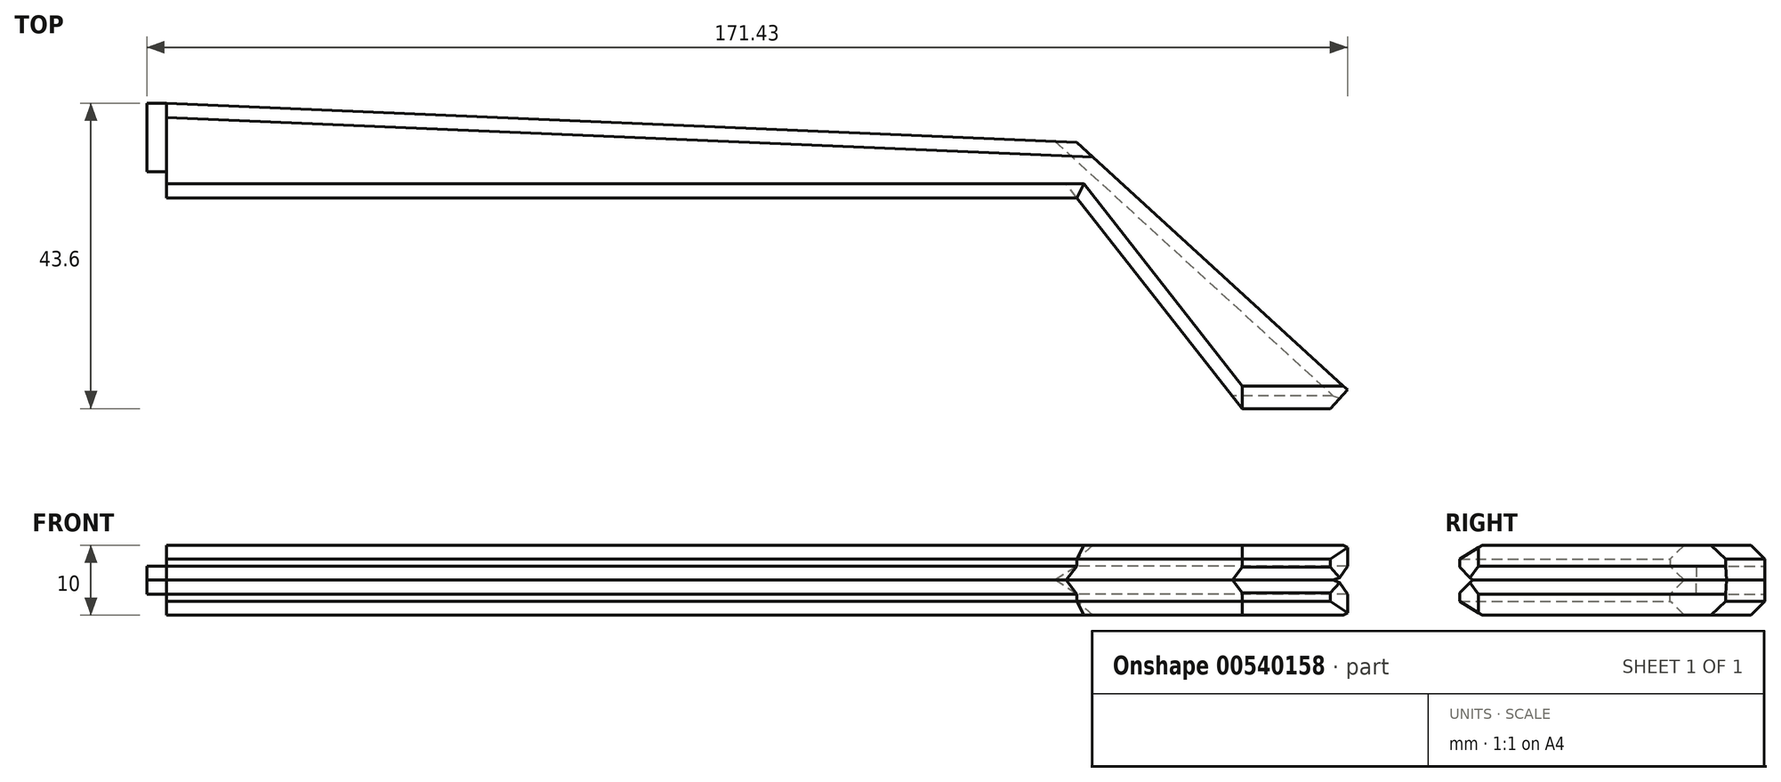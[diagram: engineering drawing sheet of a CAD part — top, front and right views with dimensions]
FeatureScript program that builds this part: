
annotation { "Feature Type Name" : "Feature", "Feature Type Description" : "" }
export const myFeature = defineFeature(function(context is Context, id is Id, definition is map)
    precondition{}
    {
        {
            var Q0;
            Q0=qCreatedBy(makeId("Top.planeOp"),FACE);
            var sketch = newSketch(context, id + "F0", { "sketchPlane" : qUnion([Q0])});
            skLineSegment(sketch, "E0", {"start": v(-80.29, 29.32) * mm, "end": v(49.71, 23.74) * mm});
            skLineSegment(sketch, "E1", {"start": v(49.71, 23.74) * mm, "end": v(88.34, -11.6) * mm});
            skLineSegment(sketch, "E2", {"start": v(88.34, -11.6) * mm, "end": v(85.75, -14.44) * mm});
            skLineSegment(sketch, "E3", {"start": v(85.75, -14.44) * mm, "end": v(73.34, -14.44) * mm});
            skLineSegment(sketch, "E4", {"start": v(73.34, -14.44) * mm, "end": v(73.34, -14.28) * mm});
            skLineSegment(sketch, "E5", {"start": v(73.34, -14.28) * mm, "end": v(49.71, 15.8) * mm});
            skLineSegment(sketch, "E6", {"start": v(49.71, 15.8) * mm, "end": v(-80.29, 15.8) * mm});
            skLineSegment(sketch, "E7", {"start": v(-80.29, 15.8) * mm, "end": v(-80.29, 29.32) * mm});
            skLineSegment(sketch, "E8", {"start": v(-80.29, 29.32) * mm, "end": v(-83.09, 29.32) * mm});
            skLineSegment(sketch, "E9", {"start": v(-83.09, 29.32) * mm, "end": v(-83.09, 19.52) * mm});
            skLineSegment(sketch, "E10", {"start": v(-83.09, 19.52) * mm, "end": v(-80.29, 19.52) * mm});
            skLineSegment(sketch, "E11", {"start": v(-80.29, 29.32) * mm, "end": v(-80.29, 19.52) * mm});
            skSolve(sketch);
        }
        {
            var Q0;
            {var subQ0=sQuery(id+"F0.wireOp",EDGE,"E0");Q0=makeQuery(id+"F0.imprint","IMPRINT",FACE,{"disambiguationData":[TD([[makeQuery(id+"F0.imprint","IMPRINT",EDGE,{"derivedFrom":subQ0}),-1.0]])]});}
            extrude(context, id + "F1", {"entities" : qUnion([Q0]), "depth" : 5 * mm, "offsetDistance" : 25 * mm});
        }
        {
            var Q0;
            Q0=makeQuery(id+"F1.opExtrude","CAP_EDGE",EDGE,{"disambiguationData":[OSD([sQuery(id+"F0.wireOp",EDGE,"E6")])],"isStart":true});
            var Q1;
            Q1=makeQuery(id+"F1.opExtrude","CAP_EDGE",EDGE,{"disambiguationData":[OSD([sQuery(id+"F0.wireOp",EDGE,"E1")])],"isStart":true});
            var Q2;
            Q2=makeQuery(id+"F1.opExtrude","CAP_EDGE",EDGE,{"disambiguationData":[OSD([sQuery(id+"F0.wireOp",EDGE,"E3")])],"isStart":true});
            var Q3;
            Q3=makeQuery(id+"F1.opExtrude","CAP_EDGE",EDGE,{"disambiguationData":[OSD([sQuery(id+"F0.wireOp",EDGE,"E5")])],"isStart":false});
            var Q4;
            Q4=makeQuery(id+"F1.opExtrude","CAP_EDGE",EDGE,{"disambiguationData":[OSD([sQuery(id+"F0.wireOp",EDGE,"E6")])],"isStart":false});
            var Q5;
            Q5=makeQuery(id+"F1.opExtrude","CAP_EDGE",EDGE,{"disambiguationData":[OSD([sQuery(id+"F0.wireOp",EDGE,"E0")])],"isStart":false});
            chamfer(context, id + "F2", {"entities" : qUnion([Q0, Q1, Q2, Q3, Q4, Q5]), "width" : 2 * mm, "tangentPropagation" : true});
        }
        {
            var Q0;
            Q0=makeQuery(id+"F0.imprint","IMPRINT",FACE,{"disambiguationData":[TD([[makeQuery(id+"F0.imprint","IMPRINT",EDGE,{"derivedFrom":sQuery(id+"F0.wireOp",EDGE,"E8")}),1.0]])]});
            extrude(context, id + "F3", {"entities" : qUnion([Q0]), "operationType" : NewBodyOperationType.ADD, "depth" : 2 * mm, "offsetDistance" : 25 * mm});
        }
        {
            var Q0;
            Q0=makeQuery(id+"F1.opExtrude","SWEPT_BODY",BODY,{"disambiguationData":[OSD([sQuery(id+"F0.wireOp",EDGE,"E0"),sQuery(id+"F0.wireOp",EDGE,"E1"),sQuery(id+"F0.wireOp",EDGE,"E2"),sQuery(id+"F0.wireOp",EDGE,"E3"),sQuery(id+"F0.wireOp",EDGE,"E4"),sQuery(id+"F0.wireOp",EDGE,"E5"),sQuery(id+"F0.wireOp",EDGE,"E6"),sQuery(id+"F0.wireOp",EDGE,"E7"),sQuery(id+"F0.wireOp",EDGE,"E11")])]});
            var Q1;
            Q1=qCreatedBy(makeId("Top.planeOp"),FACE);
            mirror(context, id + "F4", {"entities" : qUnion([Q0]), "mirrorPlane" : qUnion([Q1])});
        }
        {
            var Q0;
            Q0=makeQuery(id+"F1.opExtrude","SWEPT_FACE",FACE,{"disambiguationData":[OSD([sQuery(id+"F0.wireOp",EDGE,"E4")])]});
            extrude(context, id + "F5", {"entities" : qUnion([Q0]), "operationType" : NewBodyOperationType.REMOVE, "oppositeDirection" : true, "depth" : 25 * mm, "offsetDistance" : 25 * mm});
        }
        {
            var Q0;
            Q0=makeQuery(id+"F4.opPattern","COPY",FACE,{"derivedFrom":makeQuery(id+"F1.opExtrude","SWEPT_FACE",FACE,{"disambiguationData":[OSD([sQuery(id+"F0.wireOp",EDGE,"E4")])]}),"instanceName":"1"});
            extrude(context, id + "F6", {"entities" : qUnion([Q0]), "operationType" : NewBodyOperationType.REMOVE, "oppositeDirection" : true, "depth" : 25 * mm, "offsetDistance" : 25 * mm});
        }
    });
